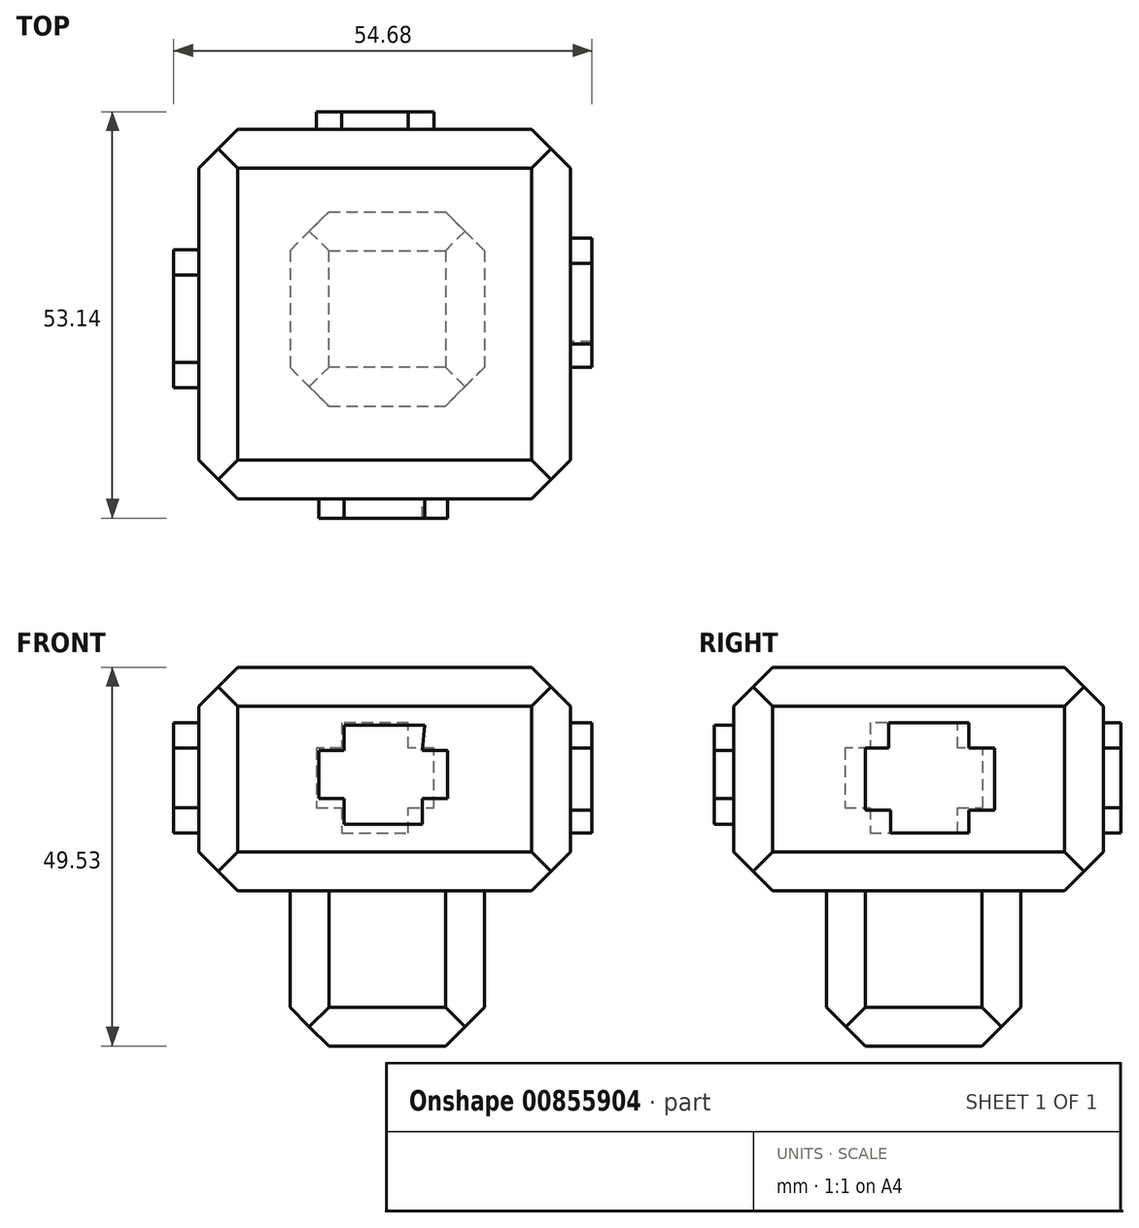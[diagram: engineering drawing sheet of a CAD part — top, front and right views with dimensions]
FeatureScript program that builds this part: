
annotation { "Feature Type Name" : "Feature", "Feature Type Description" : "" }
export const myFeature = defineFeature(function(context is Context, id is Id, definition is map)
    precondition{}
    {
        {
            var Q0;
            Q0=qCreatedBy(makeId("Top.planeOp"),FACE);
            var sketch = newSketch(context, id + "F0", { "sketchPlane" : qUnion([Q0])});
            skLineSegment(sketch, "E0.bottom", {"start": v(0, 0) * mm, "end": v(25.42, 0) * mm});
            skLineSegment(sketch, "E0.top", {"start": v(0, -25.42) * mm, "end": v(25.42, -25.42) * mm});
            skLineSegment(sketch, "E0.left", {"start": v(0, 0) * mm, "end": v(0, -25.42) * mm});
            skLineSegment(sketch, "E0.right", {"start": v(25.42, 0) * mm, "end": v(25.42, -25.42) * mm});
            skSolve(sketch);
        }
        {
            var Q0;
            Q0 = qSketchRegion(id + "F0", true);
            extrude(context, id + "F1", {"entities" : qUnion([Q0]), "depth" : 26.42 * mm, "offsetDistance" : 25.4 * mm});
        }
        {
            var Q0;
            Q0=makeQuery(id+"F1.opExtrude","CAP_EDGE",EDGE,{"disambiguationData":[OSD([sQuery(id+"F0.wireOp",EDGE,"E0.top")])],"isStart":true});
            chamfer(context, id + "F2", {"entities" : qUnion([Q0]), "width" : 5.08 * mm, "tangentPropagation" : true});
        }
        {
            var Q0;
            Q0=makeQuery(id+"F1.opExtrude","CAP_EDGE",EDGE,{"disambiguationData":[OSD([sQuery(id+"F0.wireOp",EDGE,"E0.bottom")])],"isStart":true});
            chamfer(context, id + "F3", {"entities" : qUnion([Q0]), "width" : 5.08 * mm, "tangentPropagation" : true});
        }
        {
            var Q0;
            Q0=makeQuery(id+"F1.opExtrude","CAP_EDGE",EDGE,{"disambiguationData":[OSD([sQuery(id+"F0.wireOp",EDGE,"E0.bottom")])],"isStart":false});
            chamfer(context, id + "F4", {"entities" : qUnion([Q0]), "width" : 5.08 * mm, "tangentPropagation" : true});
        }
        {
            var Q0;
            Q0=makeQuery(id+"F1.opExtrude","CAP_EDGE",EDGE,{"disambiguationData":[OSD([sQuery(id+"F0.wireOp",EDGE,"E0.top")])],"isStart":false});
            chamfer(context, id + "F5", {"entities" : qUnion([Q0]), "width" : 5.08 * mm, "tangentPropagation" : true});
        }
        {
            var Q0;
            Q0=makeQuery(id+"F1.opExtrude","SWEPT_EDGE",EDGE,{"disambiguationData":[OSD([sQuery(id+"F0.wireOp",EDGE,"E0.bottom"),sQuery(id+"F0.wireOp",EDGE,"E0.right")])]});
            chamfer(context, id + "F6", {"entities" : qUnion([Q0]), "width" : 5.08 * mm, "tangentPropagation" : true});
        }
        {
            var Q0;
            Q0=makeQuery(id+"F1.opExtrude","SWEPT_EDGE",EDGE,{"disambiguationData":[OSD([sQuery(id+"F0.wireOp",EDGE,"E0.bottom"),sQuery(id+"F0.wireOp",EDGE,"E0.left")])]});
            chamfer(context, id + "F7", {"entities" : qUnion([Q0]), "width" : 5.08 * mm, "tangentPropagation" : true});
        }
        {
            var Q0;
            Q0=makeQuery(id+"F1.opExtrude","SWEPT_EDGE",EDGE,{"disambiguationData":[OSD([sQuery(id+"F0.wireOp",EDGE,"E0.top"),sQuery(id+"F0.wireOp",EDGE,"E0.left")])]});
            chamfer(context, id + "F8", {"entities" : qUnion([Q0]), "width" : 5.08 * mm, "tangentPropagation" : true});
        }
        {
            var Q0;
            Q0=makeQuery(id+"F1.opExtrude","SWEPT_EDGE",EDGE,{"disambiguationData":[OSD([sQuery(id+"F0.wireOp",EDGE,"E0.top"),sQuery(id+"F0.wireOp",EDGE,"E0.right")])]});
            chamfer(context, id + "F9", {"entities" : qUnion([Q0]), "width" : 5.08 * mm, "tangentPropagation" : true});
        }
        {
            var Q0;
            Q0=makeQuery(id+"F1.opExtrude","CAP_EDGE",EDGE,{"disambiguationData":[OSD([sQuery(id+"F0.wireOp",EDGE,"E0.right")])],"isStart":true});
            chamfer(context, id + "F10", {"entities" : qUnion([Q0]), "width" : 5.08 * mm, "tangentPropagation" : true});
        }
        {
            var Q0;
            Q0=makeQuery(id+"F1.opExtrude","CAP_EDGE",EDGE,{"disambiguationData":[OSD([sQuery(id+"F0.wireOp",EDGE,"E0.right")])],"isStart":false});
            chamfer(context, id + "F11", {"entities" : qUnion([Q0]), "width" : 5.08 * mm, "tangentPropagation" : true});
        }
        {
            var Q0;
            Q0=makeQuery(id+"F1.opExtrude","CAP_EDGE",EDGE,{"disambiguationData":[OSD([sQuery(id+"F0.wireOp",EDGE,"E0.left")])],"isStart":true});
            chamfer(context, id + "F12", {"entities" : qUnion([Q0]), "width" : 5.08 * mm, "tangentPropagation" : true});
        }
        {
            var Q0;
            Q0=makeQuery(id+"F1.opExtrude","CAP_EDGE",EDGE,{"disambiguationData":[OSD([sQuery(id+"F0.wireOp",EDGE,"E0.left")])],"isStart":false});
            chamfer(context, id + "F13", {"entities" : qUnion([Q0]), "width" : 5.08 * mm, "tangentPropagation" : true});
        }
        {
            var Q0;
            Q0=makeQuery(id+"F1.opExtrude","CAP_FACE",FACE,{"disambiguationData":[OSD([sQuery(id+"F0.wireOp",EDGE,"E0.bottom"),sQuery(id+"F0.wireOp",EDGE,"E0.top"),sQuery(id+"F0.wireOp",EDGE,"E0.left"),sQuery(id+"F0.wireOp",EDGE,"E0.right")])],"isStart":false});
            var sketch = newSketch(context, id + "F14", { "sketchPlane" : qUnion([Q0])});
            skLineSegment(sketch, "E1.bottom", {"start": v(-11.9, 10.8) * mm, "end": v(36.7, 10.8) * mm});
            skLineSegment(sketch, "E1.top", {"start": v(-11.9, -37.51) * mm, "end": v(36.7, -37.51) * mm});
            skLineSegment(sketch, "E1.left", {"start": v(-11.9, 10.8) * mm, "end": v(-11.9, -37.51) * mm});
            skLineSegment(sketch, "E1.right", {"start": v(36.7, 10.8) * mm, "end": v(36.7, -37.51) * mm});
            skSolve(sketch);
        }
        {
            var Q0;
            Q0 = qSketchRegion(id + "F14", true);
            extrude(context, id + "F15", {"entities" : qUnion([Q0]), "operationType" : NewBodyOperationType.ADD, "oppositeDirection" : true, "depth" : 6.1 * mm, "offsetDistance" : 25.4 * mm});
        }
        {
            var Q0;
            Q0=makeQuery(id+"F15.boolean.opBoolean","MERGE",FACE,{"derivedFrom":[makeQuery(id+"F1.opExtrude","CAP_FACE",FACE,{"disambiguationData":[OSD([sQuery(id+"F0.wireOp",EDGE,"E0.bottom"),sQuery(id+"F0.wireOp",EDGE,"E0.top"),sQuery(id+"F0.wireOp",EDGE,"E0.left"),sQuery(id+"F0.wireOp",EDGE,"E0.right")])],"isStart":false}),makeQuery(id+"F15.opExtrude","CAP_FACE",FACE,{"disambiguationData":[OSD([sQuery(id+"F14.wireOp",EDGE,"E1.bottom"),sQuery(id+"F14.wireOp",EDGE,"E1.top"),sQuery(id+"F14.wireOp",EDGE,"E1.left"),sQuery(id+"F14.wireOp",EDGE,"E1.right")])],"isStart":true})]});
            extrude(context, id + "F16", {"entities" : qUnion([Q0]), "operationType" : NewBodyOperationType.ADD, "depth" : 23.1 * mm, "offsetDistance" : 25.4 * mm});
        }
        {
            var Q0;
            {var subQ0=sQuery(id+"F14.wireOp",EDGE,"E1.left");var subQ1=sQuery(id+"F14.wireOp",EDGE,"E1.top");Q0=makeQuery(id+"F16.boolean.opBoolean","MERGE",EDGE,{"derivedFrom":[makeQuery(id+"F15.opExtrude","SWEPT_EDGE",EDGE,{"disambiguationData":[OSD([subQ1,subQ0])]}),makeQuery(id+"F16.opExtrude","SWEPT_EDGE",EDGE,{"disambiguationData":[OSD([subQ1,subQ0])]})]});}
            chamfer(context, id + "F17", {"entities" : qUnion([Q0]), "width" : 5.08 * mm, "tangentPropagation" : true});
        }
        {
            var Q0;
            Q0=makeQuery(id+"F16.opExtrude","CAP_EDGE",EDGE,{"disambiguationData":[OSD([sQuery(id+"F14.wireOp",EDGE,"E1.top")])],"isStart":false});
            var Q1;
            Q1=makeQuery(id+"F15.opExtrude","CAP_EDGE",EDGE,{"disambiguationData":[OSD([sQuery(id+"F14.wireOp",EDGE,"E1.top")])],"isStart":false});
            chamfer(context, id + "F18", {"entities" : qUnion([Q0, Q1]), "width" : 5.08 * mm, "tangentPropagation" : true});
        }
        {
            var Q0;
            {var subQ0=sQuery(id+"F14.wireOp",EDGE,"E1.right");var subQ1=sQuery(id+"F14.wireOp",EDGE,"E1.top");Q0=makeQuery(id+"F16.boolean.opBoolean","MERGE",EDGE,{"derivedFrom":[makeQuery(id+"F15.opExtrude","SWEPT_EDGE",EDGE,{"disambiguationData":[OSD([subQ1,subQ0])]}),makeQuery(id+"F16.opExtrude","SWEPT_EDGE",EDGE,{"disambiguationData":[OSD([subQ1,subQ0])]})]});}
            chamfer(context, id + "F19", {"entities" : qUnion([Q0]), "width" : 5.08 * mm, "tangentPropagation" : true});
        }
        {
            var Q0;
            Q0=makeQuery(id+"F16.opExtrude","CAP_EDGE",EDGE,{"disambiguationData":[OSD([sQuery(id+"F14.wireOp",EDGE,"E1.right")])],"isStart":false});
            chamfer(context, id + "F20", {"entities" : qUnion([Q0]), "width" : 5.08 * mm, "tangentPropagation" : true});
        }
        {
            var Q0;
            Q0=makeQuery(id+"F15.opExtrude","CAP_EDGE",EDGE,{"disambiguationData":[OSD([sQuery(id+"F14.wireOp",EDGE,"E1.right")])],"isStart":false});
            chamfer(context, id + "F21", {"entities" : qUnion([Q0]), "width" : 5.08 * mm, "tangentPropagation" : true});
        }
        {
            var Q0;
            {var subQ0=sQuery(id+"F14.wireOp",EDGE,"E1.right");var subQ1=sQuery(id+"F14.wireOp",EDGE,"E1.bottom");Q0=makeQuery(id+"F16.boolean.opBoolean","MERGE",EDGE,{"derivedFrom":[makeQuery(id+"F15.opExtrude","SWEPT_EDGE",EDGE,{"disambiguationData":[OSD([subQ1,subQ0])]}),makeQuery(id+"F16.opExtrude","SWEPT_EDGE",EDGE,{"disambiguationData":[OSD([subQ1,subQ0])]})]});}
            chamfer(context, id + "F22", {"entities" : qUnion([Q0]), "width" : 5.08 * mm, "tangentPropagation" : true});
        }
        {
            var Q0;
            Q0=makeQuery(id+"F16.opExtrude","CAP_EDGE",EDGE,{"disambiguationData":[OSD([sQuery(id+"F14.wireOp",EDGE,"E1.bottom")])],"isStart":false});
            chamfer(context, id + "F23", {"entities" : qUnion([Q0]), "width" : 5.08 * mm, "tangentPropagation" : true});
        }
        {
            var Q0;
            Q0=makeQuery(id+"F15.opExtrude","CAP_EDGE",EDGE,{"disambiguationData":[OSD([sQuery(id+"F14.wireOp",EDGE,"E1.bottom")])],"isStart":false});
            chamfer(context, id + "F24", {"entities" : qUnion([Q0]), "width" : 5.08 * mm, "tangentPropagation" : true});
        }
        {
            var Q0;
            {var subQ0=sQuery(id+"F14.wireOp",EDGE,"E1.left");var subQ1=sQuery(id+"F14.wireOp",EDGE,"E1.bottom");Q0=makeQuery(id+"F16.boolean.opBoolean","MERGE",EDGE,{"derivedFrom":[makeQuery(id+"F15.opExtrude","SWEPT_EDGE",EDGE,{"disambiguationData":[OSD([subQ1,subQ0])]}),makeQuery(id+"F16.opExtrude","SWEPT_EDGE",EDGE,{"disambiguationData":[OSD([subQ1,subQ0])]})]});}
            chamfer(context, id + "F25", {"entities" : qUnion([Q0]), "width" : 5.08 * mm, "tangentPropagation" : true});
        }
        {
            var Q0;
            Q0=makeQuery(id+"F16.opExtrude","CAP_EDGE",EDGE,{"disambiguationData":[OSD([sQuery(id+"F14.wireOp",EDGE,"E1.left")])],"isStart":false});
            chamfer(context, id + "F26", {"entities" : qUnion([Q0]), "width" : 5.08 * mm, "tangentPropagation" : true});
        }
        {
            var Q0;
            Q0=makeQuery(id+"F15.opExtrude","CAP_EDGE",EDGE,{"disambiguationData":[OSD([sQuery(id+"F14.wireOp",EDGE,"E1.left")])],"isStart":false});
            chamfer(context, id + "F27", {"entities" : qUnion([Q0]), "width" : 5.08 * mm, "tangentPropagation" : true});
        }
        {
            var Q0;
            {var subQ0=sQuery(id+"F14.wireOp",EDGE,"E1.top");Q0=makeQuery(id+"F16.boolean.opBoolean","MERGE",FACE,{"derivedFrom":[makeQuery(id+"F15.opExtrude","SWEPT_FACE",FACE,{"disambiguationData":[OSD([subQ0])]}),makeQuery(id+"F16.opExtrude","SWEPT_FACE",FACE,{"disambiguationData":[OSD([subQ0])]})]});}
            var sketch = newSketch(context, id + "F28", { "sketchPlane" : qUnion([Q0])});
            skLineSegment(sketch, "E2", {"start": v(7.07, 41.96) * mm, "end": v(17.6, 41.96) * mm});
            skLineSegment(sketch, "E3", {"start": v(7.07, 41.96) * mm, "end": v(7.07, 38.65) * mm});
            skLineSegment(sketch, "E4", {"start": v(7.07, 38.65) * mm, "end": v(3.76, 38.65) * mm});
            skLineSegment(sketch, "E5", {"start": v(3.76, 38.65) * mm, "end": v(3.76, 32.33) * mm});
            skLineSegment(sketch, "E6", {"start": v(3.76, 32.33) * mm, "end": v(7.07, 32.33) * mm});
            skLineSegment(sketch, "E7", {"start": v(7.07, 32.33) * mm, "end": v(7.07, 29.03) * mm});
            skLineSegment(sketch, "E8", {"start": v(7.07, 29.03) * mm, "end": v(17.3, 29.03) * mm});
            skLineSegment(sketch, "E9", {"start": v(17.3, 29.03) * mm, "end": v(17.3, 32.33) * mm});
            skLineSegment(sketch, "E10", {"start": v(17.3, 32.33) * mm, "end": v(20.6, 32.33) * mm});
            skLineSegment(sketch, "E11", {"start": v(20.6, 32.33) * mm, "end": v(20.6, 38.65) * mm});
            skLineSegment(sketch, "E12", {"start": v(20.6, 38.65) * mm, "end": v(17.3, 38.65) * mm});
            skLineSegment(sketch, "E13", {"start": v(17.3, 38.65) * mm, "end": v(17.6, 41.96) * mm});
            skSolve(sketch);
        }
        {
            var Q0;
            Q0=makeQuery(id+"F28.imprint","IMPRINT",FACE,{"disambiguationData":[TD([[makeQuery(id+"F28.imprint","IMPRINT",EDGE,{"derivedFrom":sQuery(id+"F28.wireOp",EDGE,"E2")}),-1.0]])]});
            extrude(context, id + "F29", {"entities" : qUnion([Q0]), "operationType" : NewBodyOperationType.ADD, "depth" : 2.54 * mm, "offsetDistance" : 25.4 * mm});
        }
        {
            var Q0;
            {var subQ0=sQuery(id+"F14.wireOp",EDGE,"E1.bottom");Q0=makeQuery(id+"F16.boolean.opBoolean","MERGE",FACE,{"derivedFrom":[makeQuery(id+"F15.opExtrude","SWEPT_FACE",FACE,{"disambiguationData":[OSD([subQ0])]}),makeQuery(id+"F16.opExtrude","SWEPT_FACE",FACE,{"disambiguationData":[OSD([subQ0])]})]});}
            var sketch = newSketch(context, id + "F30", { "sketchPlane" : qUnion([Q0])});
            skLineSegment(sketch, "E14", {"start": v(-6.77, 42.26) * mm, "end": v(-6.77, 38.95) * mm});
            skLineSegment(sketch, "E15", {"start": v(-6.77, 38.95) * mm, "end": v(-3.46, 38.95) * mm});
            skLineSegment(sketch, "E16", {"start": v(-3.46, 38.95) * mm, "end": v(-3.46, 31.13) * mm});
            skLineSegment(sketch, "E17", {"start": v(-3.46, 31.13) * mm, "end": v(-6.77, 31.13) * mm});
            skLineSegment(sketch, "E18", {"start": v(-6.77, 31.13) * mm, "end": v(-6.77, 27.82) * mm});
            skLineSegment(sketch, "E19", {"start": v(-6.77, 27.82) * mm, "end": v(-15.5, 27.82) * mm});
            skLineSegment(sketch, "E20", {"start": v(-15.5, 27.82) * mm, "end": v(-15.5, 31.13) * mm});
            skLineSegment(sketch, "E21", {"start": v(-15.5, 31.13) * mm, "end": v(-18.8, 31.13) * mm});
            skLineSegment(sketch, "E22", {"start": v(-18.8, 31.13) * mm, "end": v(-18.8, 38.95) * mm});
            skLineSegment(sketch, "E23", {"start": v(-18.8, 38.95) * mm, "end": v(-15.5, 38.95) * mm});
            skLineSegment(sketch, "E24", {"start": v(-15.5, 38.95) * mm, "end": v(-15.5, 42.26) * mm});
            skLineSegment(sketch, "E25", {"start": v(-15.5, 42.26) * mm, "end": v(-6.77, 42.26) * mm});
            skSolve(sketch);
        }
        {
            var Q0;
            Q0=makeQuery(id+"F30.imprint","IMPRINT",FACE,{"disambiguationData":[TD([[makeQuery(id+"F30.imprint","IMPRINT",EDGE,{"derivedFrom":sQuery(id+"F30.wireOp",EDGE,"E14")}),-1.0]])]});
            extrude(context, id + "F31", {"entities" : qUnion([Q0]), "operationType" : NewBodyOperationType.ADD, "depth" : 2.3 * mm, "offsetDistance" : 25.4 * mm});
        }
        {
            var Q0;
            {var subQ0=sQuery(id+"F14.wireOp",EDGE,"E1.right");Q0=makeQuery(id+"F16.boolean.opBoolean","MERGE",FACE,{"derivedFrom":[makeQuery(id+"F15.opExtrude","SWEPT_FACE",FACE,{"disambiguationData":[OSD([subQ0])]}),makeQuery(id+"F16.opExtrude","SWEPT_FACE",FACE,{"disambiguationData":[OSD([subQ0])]})]});}
            var sketch = newSketch(context, id + "F32", { "sketchPlane" : qUnion([Q0])});
            skLineSegment(sketch, "E26", {"start": v(-6.77, 42.26) * mm, "end": v(-17.3, 42.26) * mm});
            skLineSegment(sketch, "E27", {"start": v(-6.77, 42.26) * mm, "end": v(-6.77, 38.95) * mm});
            skLineSegment(sketch, "E28", {"start": v(-6.77, 38.95) * mm, "end": v(-3.46, 38.95) * mm});
            skLineSegment(sketch, "E29", {"start": v(-3.46, 38.95) * mm, "end": v(-3.46, 30.83) * mm});
            skLineSegment(sketch, "E30", {"start": v(-3.46, 30.83) * mm, "end": v(-6.77, 30.83) * mm});
            skLineSegment(sketch, "E31", {"start": v(-6.77, 30.83) * mm, "end": v(-6.77, 27.82) * mm});
            skLineSegment(sketch, "E32", {"start": v(-6.77, 27.82) * mm, "end": v(-17, 27.82) * mm});
            skLineSegment(sketch, "E33", {"start": v(-17, 27.82) * mm, "end": v(-17, 30.83) * mm});
            skLineSegment(sketch, "E34", {"start": v(-17, 30.83) * mm, "end": v(-20.3, 30.83) * mm});
            skLineSegment(sketch, "E35", {"start": v(-20.3, 30.83) * mm, "end": v(-20.3, 38.95) * mm});
            skLineSegment(sketch, "E36", {"start": v(-17.3, 42.26) * mm, "end": v(-17.3, 38.95) * mm});
            skLineSegment(sketch, "E37", {"start": v(-17.3, 38.95) * mm, "end": v(-20.3, 38.95) * mm});
            skSolve(sketch);
        }
        {
            var Q0;
            Q0=makeQuery(id+"F32.imprint","IMPRINT",FACE,{"disambiguationData":[TD([[makeQuery(id+"F32.imprint","IMPRINT",EDGE,{"derivedFrom":sQuery(id+"F32.wireOp",EDGE,"E26")}),1.0]])]});
            extrude(context, id + "F33", {"entities" : qUnion([Q0]), "operationType" : NewBodyOperationType.ADD, "depth" : 2.8 * mm, "offsetDistance" : 25.4 * mm});
        }
        {
            var Q0;
            {var subQ0=sQuery(id+"F14.wireOp",EDGE,"E1.left");Q0=makeQuery(id+"F16.boolean.opBoolean","MERGE",FACE,{"derivedFrom":[makeQuery(id+"F15.opExtrude","SWEPT_FACE",FACE,{"disambiguationData":[OSD([subQ0])]}),makeQuery(id+"F16.opExtrude","SWEPT_FACE",FACE,{"disambiguationData":[OSD([subQ0])]})]});}
            var sketch = newSketch(context, id + "F34", { "sketchPlane" : qUnion([Q0])});
            skLineSegment(sketch, "E38", {"start": v(8.27, 42.26) * mm, "end": v(19.7, 42.26) * mm});
            skLineSegment(sketch, "E39", {"start": v(19.7, 42.26) * mm, "end": v(19.7, 38.95) * mm});
            skLineSegment(sketch, "E40", {"start": v(19.7, 38.95) * mm, "end": v(23.01, 38.95) * mm});
            skLineSegment(sketch, "E41", {"start": v(23.01, 38.95) * mm, "end": v(23.01, 31.13) * mm});
            skLineSegment(sketch, "E42", {"start": v(23.01, 31.13) * mm, "end": v(19.7, 31.13) * mm});
            skLineSegment(sketch, "E43", {"start": v(19.7, 31.13) * mm, "end": v(19.7, 27.82) * mm});
            skLineSegment(sketch, "E44", {"start": v(19.7, 27.82) * mm, "end": v(8.27, 27.82) * mm});
            skLineSegment(sketch, "E45", {"start": v(8.27, 27.82) * mm, "end": v(8.27, 31.13) * mm});
            skLineSegment(sketch, "E46", {"start": v(8.27, 31.13) * mm, "end": v(4.96, 31.13) * mm});
            skLineSegment(sketch, "E47", {"start": v(4.96, 31.13) * mm, "end": v(4.96, 38.95) * mm});
            skLineSegment(sketch, "E48", {"start": v(4.96, 38.95) * mm, "end": v(8.27, 38.95) * mm});
            skLineSegment(sketch, "E49", {"start": v(8.27, 38.95) * mm, "end": v(8.27, 42.26) * mm});
            skSolve(sketch);
        }
        {
            var Q0;
            Q0=makeQuery(id+"F34.imprint","IMPRINT",FACE,{"disambiguationData":[TD([[makeQuery(id+"F34.imprint","IMPRINT",EDGE,{"derivedFrom":sQuery(id+"F34.wireOp",EDGE,"E38")}),-1.0]])]});
            extrude(context, id + "F35", {"entities" : qUnion([Q0]), "operationType" : NewBodyOperationType.ADD, "depth" : 3.3 * mm, "offsetDistance" : 25.4 * mm});
        }
    });
